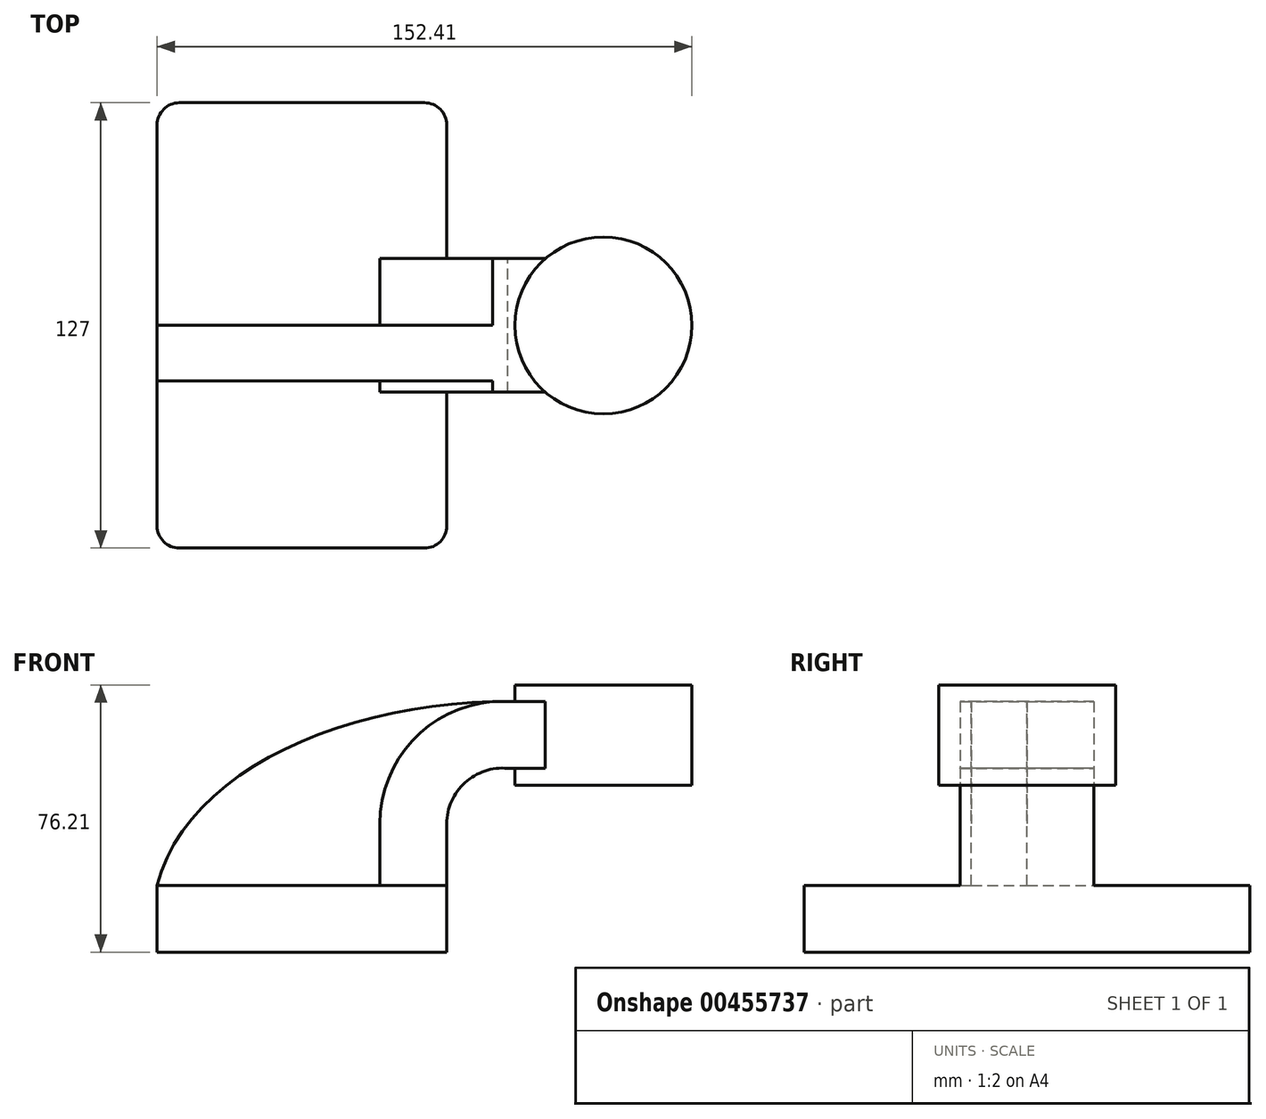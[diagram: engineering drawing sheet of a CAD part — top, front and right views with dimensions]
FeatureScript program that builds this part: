
annotation { "Feature Type Name" : "Feature", "Feature Type Description" : "" }
export const myFeature = defineFeature(function(context is Context, id is Id, definition is map)
    precondition{}
    {
        {
            var Q0;
            Q0=qCreatedBy(makeId("Front.planeOp"),FACE);
            var sketch = newSketch(context, id + "F0", { "sketchPlane" : qUnion([Q0])});
            skLineSegment(sketch, "E0.bottom", {"start": v(41.28, -9.52) * mm, "end": v(-41.28, -9.53) * mm});
            skLineSegment(sketch, "E0.top", {"start": v(41.28, 9.53) * mm, "end": v(-41.28, 9.53) * mm});
            skLineSegment(sketch, "E0.left", {"start": v(41.28, -9.52) * mm, "end": v(41.28, 9.53) * mm});
            skLineSegment(sketch, "E0.right", {"start": v(-41.28, -9.53) * mm, "end": v(-41.28, 9.53) * mm});
            skPoint(sketch, "E0.middle", {"position": v(0, 0) * mm});
            skLineSegment(sketch, "E1.bottom", {"start": v(111.12, 66.68) * mm, "end": v(60.32, 66.68) * mm});
            skLineSegment(sketch, "E1.top", {"start": v(111.12, 38.1) * mm, "end": v(60.32, 38.1) * mm});
            skLineSegment(sketch, "E1.left", {"start": v(111.12, 66.68) * mm, "end": v(111.12, 38.1) * mm});
            skLineSegment(sketch, "E1.right", {"start": v(60.32, 66.67) * mm, "end": v(60.32, 38.1) * mm});
            skPoint(sketch, "E1.middle", {"position": v(85.72, 52.39) * mm});
            skLineSegment(sketch, "E2", {"start": v(41.28, 9.53) * mm, "end": v(41.28, 27.07) * mm});
            skArc(sketch, "E3", {"start": v(41.27, 27.07) * mm, "mid": v(46.46, 38.8) * mm, "end": v(58.63, 42.88) * mm});
            skLineSegment(sketch, "E4", {"start": v(58.63, 42.88) * mm, "end": v(85.9, 42.88) * mm});
            skLineSegment(sketch, "E5.0", {"start": v(59.35, 61.93) * mm, "end": v(86.08, 61.93) * mm});
            skArc(sketch, "E5.1", {"start": v(22.23, 27.07) * mm, "mid": v(33.24, 52.53) * mm, "end": v(59.35, 61.93) * mm});
            skLineSegment(sketch, "E5.2", {"start": v(22.22, 9.53) * mm, "end": v(22.22, 27.07) * mm});
            skLineSegment(sketch, "E6", {"start": v(85.9, 38.1) * mm, "end": v(85.9, 66.68) * mm});
            skFitSpline(sketch, "E7", {"points": [v(-41.28, 9.52) * mm, v(59.35, 61.93) * mm], "startDerivative": vector(24.87, 98.79) * mm, "endDerivative": vector(138.66, -0.87) * mm});
            skSolve(sketch);
        }
        {
            var Q0;
            Q0=makeQuery(id+"F0.imprint","IMPRINT",FACE,{"disambiguationData":[TD([[makeQuery(id+"F0.imprint","IMPRINT",EDGE,{"derivedFrom":sQuery(id+"F0.wireOp",EDGE,"E0.bottom")}),-1.0]])]});
            extrude(context, id + "F1", {"entities" : qUnion([Q0]), "endBound" : BoundingType.SYMMETRIC, "depth" : 127 * mm});
        }
        {
            var Q0;
            {var subQ1=sQuery(id+"F0.wireOp",EDGE,"E2");Q0=makeQuery(id+"F0.imprint","IMPRINT",FACE,{"disambiguationData":[TD([[makeQuery(id+"F0.imprint","IMPRINT",EDGE,{"derivedFrom":subQ1}),1.0]])]});}
            var Q1;
            {var subQ0=sQuery(id+"F0.wireOp",EDGE,"E5.0");var subQ1=sQuery(id+"F0.wireOp",EDGE,"E1.right");var subQ2=makeQuery(id+"F0.imprint","INTERSECT",VERTEX,{"derivedFrom":[subQ1,subQ0]});Q1=makeQuery(id+"F0.imprint","IMPRINT",FACE,{"disambiguationData":[TD([[makeQuery(id+"F0.imprint","IMPRINT",EDGE,{"disambiguationData":[TD([[subQ2,-1.0]])],"derivedFrom":subQ1}),1.0]])]});}
            extrude(context, id + "F2", {"entities" : qUnion([Q0, Q1]), "operationType" : NewBodyOperationType.ADD, "endBound" : BoundingType.SYMMETRIC, "depth" : 38.1 * mm});
        }
        {
            var Q0;
            {var subQ3=sQuery(id+"F0.wireOp",EDGE,"E5.2");Q0=makeQuery(id+"F0.imprint","IMPRINT",FACE,{"disambiguationData":[TD([[makeQuery(id+"F0.imprint","IMPRINT",EDGE,{"derivedFrom":subQ3}),1.0]])]});}
            extrude(context, id + "F3", {"entities" : qUnion([Q0]), "operationType" : NewBodyOperationType.ADD, "depth" : 15.88 * mm});
        }
        {
            var Q0;
            {var subQ0=sQuery(id+"F0.wireOp",EDGE,"E1.left");Q0=makeQuery(id+"F0.imprint","IMPRINT",FACE,{"disambiguationData":[TD([[makeQuery(id+"F0.imprint","IMPRINT",EDGE,{"derivedFrom":subQ0}),-1.0]])]});}
            var Q1;
            Q1=sQuery(id+"F0.wireOp",EDGE,"E6");
            revolve(context, id + "F4", {"operationType" : NewBodyOperationType.ADD, "entities" : qUnion([Q0]), "axis" : qUnion([Q1]), "revolveType" : RevolveType.FULL});
        }
        {
            var Q0;
            Q0=makeQuery(id+"F1.opExtrude","CAP_EDGE",EDGE,{"disambiguationData":[OSD([sQuery(id+"F0.wireOp",EDGE,"E0.right")])],"isStart":false});
            var Q1;
            Q1=makeQuery(id+"F1.opExtrude","CAP_EDGE",EDGE,{"disambiguationData":[OSD([sQuery(id+"F0.wireOp",EDGE,"E0.left")])],"isStart":false});
            var Q2;
            Q2=makeQuery(id+"F1.opExtrude","CAP_EDGE",EDGE,{"disambiguationData":[OSD([sQuery(id+"F0.wireOp",EDGE,"E0.left")])],"isStart":true});
            var Q3;
            Q3=makeQuery(id+"F1.opExtrude","CAP_EDGE",EDGE,{"disambiguationData":[OSD([sQuery(id+"F0.wireOp",EDGE,"E0.right")])],"isStart":true});
            fillet(context, id + "F5", {"entities" : qUnion([Q0, Q1, Q2, Q3]), "radius" : 6.35 * mm, "tangentPropagation" : true, "allowEdgeOverflow" : false});
        }
    });
